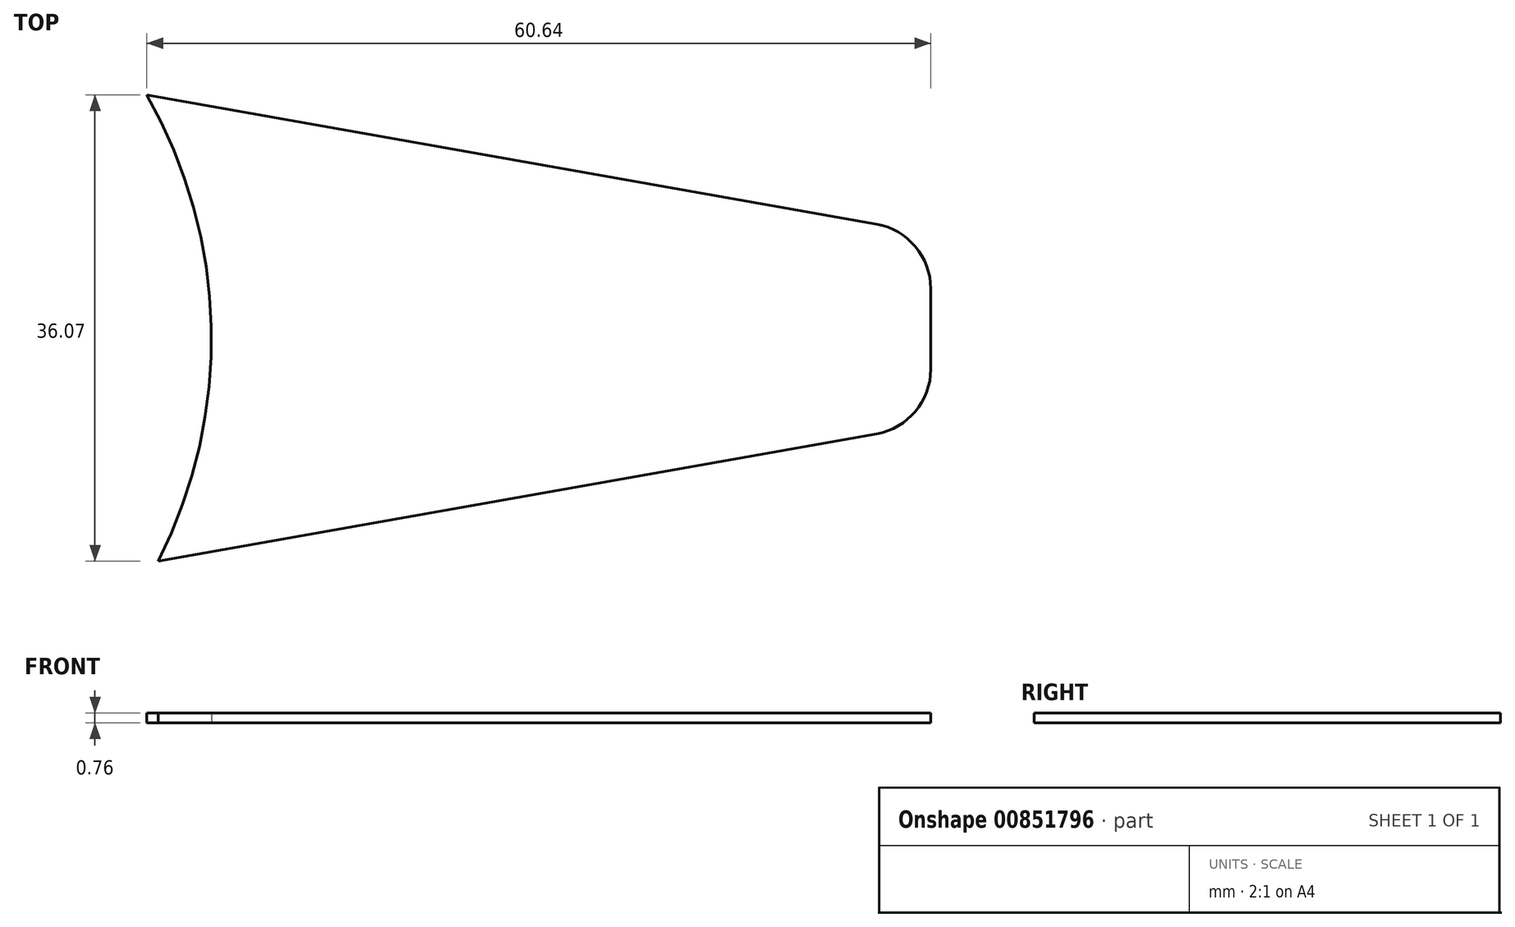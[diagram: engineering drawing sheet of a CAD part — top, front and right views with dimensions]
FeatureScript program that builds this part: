
annotation { "Feature Type Name" : "Feature", "Feature Type Description" : "" }
export const myFeature = defineFeature(function(context is Context, id is Id, definition is map)
    precondition{}
    {
        {
            var Q0;
            Q0=qCreatedBy(makeId("Top.planeOp"),FACE);
            var sketch = newSketch(context, id + "F0", { "sketchPlane" : qUnion([Q0])});
            skPoint(sketch, "E0", {"position": v(-85.77, 5.92) * mm});
            skPoint(sketch, "E1.MirrorP", {"position": v(-84.88, -30.15) * mm});
            skPoint(sketch, "E2", {"position": v(-25.13, -12.2) * mm});
            skPoint(sketch, "E3", {"position": v(-25.13, -4.83) * mm});
            skPoint(sketch, "E4.MirrorP", {"position": v(-25.13, -19.56) * mm});
            skLineSegment(sketch, "E5", {"start": v(-84.88, -30.15) * mm, "end": v(-25.13, -19.56) * mm});
            skLineSegment(sketch, "E6", {"start": v(-25.13, -4.83) * mm, "end": v(-25.13, -19.56) * mm});
            skLineSegment(sketch, "E7", {"start": v(-85.77, 5.92) * mm, "end": v(-25.13, -4.83) * mm});
            skArc(sketch, "E8", {"start": v(-84.88, -30.15) * mm, "mid": v(-80.79, -12) * mm, "end": v(-85.77, 5.92) * mm});
            skSolve(sketch);
        }
        {
            var Q0;
            Q0 = qSketchRegion(id + "F0", true);
            extrude(context, id + "F1", {"entities" : qUnion([Q0]), "endBound" : BoundingType.SYMMETRIC, "depth" : 0.76 * mm, "offsetDistance" : 25.4 * mm});
        }
        {
            var Q0;
            Q0=makeQuery(id+"F1.opExtrude","SWEPT_EDGE",EDGE,{"disambiguationData":[OSD([sQuery(id+"F0.wireOp",EDGE,"E5"),sQuery(id+"F0.wireOp",EDGE,"E6")])]});
            var Q1;
            Q1=makeQuery(id+"F1.opExtrude","SWEPT_EDGE",EDGE,{"disambiguationData":[OSD([sQuery(id+"F0.wireOp",EDGE,"E6"),sQuery(id+"F0.wireOp",EDGE,"E7")])]});
            fillet(context, id + "F2", {"entities" : qUnion([Q0, Q1]), "radius" : 5.08 * mm, "tangentPropagation" : true, "allowEdgeOverflow" : false});
        }
    });
